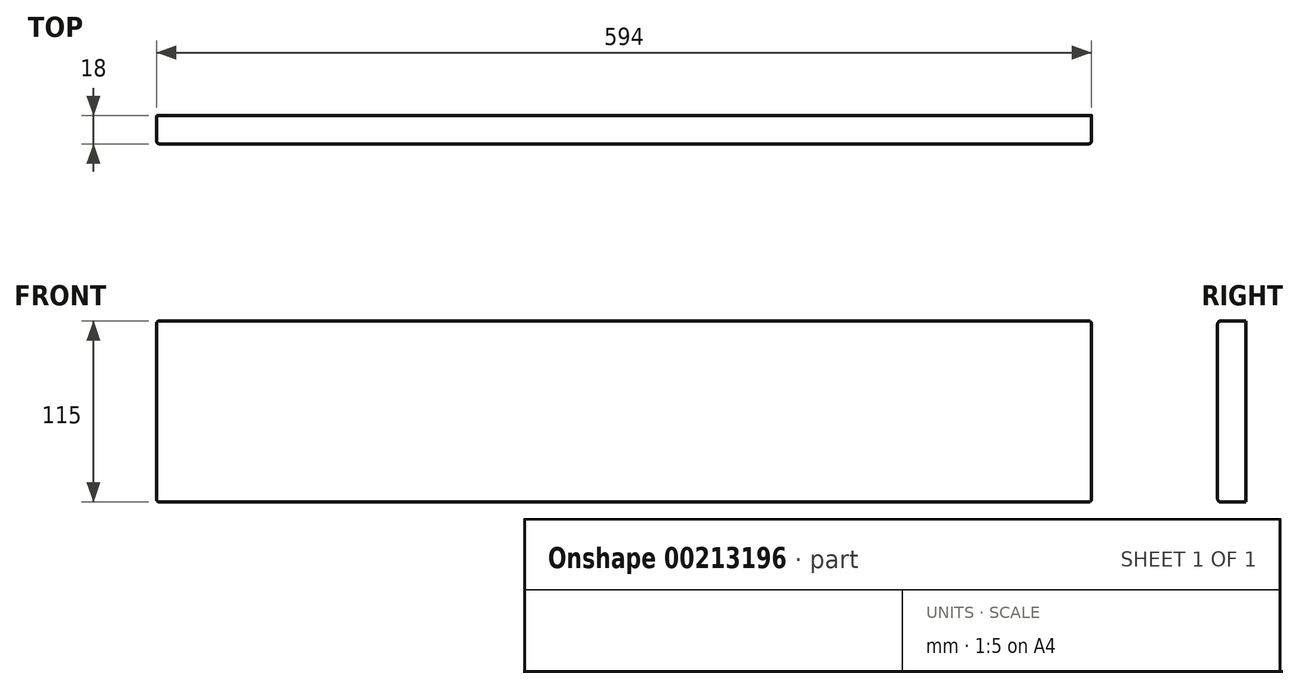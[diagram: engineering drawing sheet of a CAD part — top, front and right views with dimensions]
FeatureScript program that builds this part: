
annotation { "Feature Type Name" : "Feature", "Feature Type Description" : "" }
export const myFeature = defineFeature(function(context is Context, id is Id, definition is map)
    precondition{}
    {
        {
            var Q0;
            Q0=qCreatedBy(makeId("Front.planeOp"),FACE);
            var sketch = newSketch(context, id + "F0", { "sketchPlane" : qUnion([Q0])});
            skLineSegment(sketch, "E0.bottom", {"start": v(297, 57.5) * mm, "end": v(-297, 57.5) * mm});
            skLineSegment(sketch, "E0.top", {"start": v(297, -57.5) * mm, "end": v(-297, -57.5) * mm});
            skLineSegment(sketch, "E0.left", {"start": v(297, 57.5) * mm, "end": v(297, -57.5) * mm});
            skLineSegment(sketch, "E0.right", {"start": v(-297, 57.5) * mm, "end": v(-297, -57.5) * mm});
            skPoint(sketch, "E0.middle", {"position": v(0, 0) * mm});
            skSolve(sketch);
        }
        {
            var Q0;
            Q0=makeQuery(id+"F0.imprint","IMPRINT",FACE,{"disambiguationData":[TD([[makeQuery(id+"F0.imprint","IMPRINT",EDGE,{"derivedFrom":sQuery(id+"F0.wireOp",EDGE,"E0.bottom")}),1.0]])]});
            extrude(context, id + "F1", {"entities" : qUnion([Q0]), "endBound" : BoundingType.SYMMETRIC, "depth" : 18 * mm});
        }
        {
            var Q0;
            Q0=makeQuery(id+"F1.opExtrude","CAP_FACE",FACE,{"disambiguationData":[OSD([sQuery(id+"F0.wireOp",EDGE,"E0.bottom"),sQuery(id+"F0.wireOp",EDGE,"E0.top"),sQuery(id+"F0.wireOp",EDGE,"E0.left"),sQuery(id+"F0.wireOp",EDGE,"E0.right")])],"isStart":false});
            var Q1;
            Q1=makeQuery(id+"F1.opExtrude","SWEPT_EDGE",EDGE,{"disambiguationData":[OSD([sQuery(id+"F0.wireOp",EDGE,"E0.bottom"),sQuery(id+"F0.wireOp",EDGE,"E0.right")])]});
            var Q2;
            Q2=makeQuery(id+"F1.opExtrude","SWEPT_EDGE",EDGE,{"disambiguationData":[OSD([sQuery(id+"F0.wireOp",EDGE,"E0.top"),sQuery(id+"F0.wireOp",EDGE,"E0.right")])]});
            var Q3;
            Q3=makeQuery(id+"F1.opExtrude","SWEPT_EDGE",EDGE,{"disambiguationData":[OSD([sQuery(id+"F0.wireOp",EDGE,"E0.bottom"),sQuery(id+"F0.wireOp",EDGE,"E0.left")])]});
            var Q4;
            Q4=makeQuery(id+"F1.opExtrude","SWEPT_EDGE",EDGE,{"disambiguationData":[OSD([sQuery(id+"F0.wireOp",EDGE,"E0.top"),sQuery(id+"F0.wireOp",EDGE,"E0.left")])]});
            fillet(context, id + "F2", {"entities" : qUnion([Q0, Q1, Q2, Q3, Q4]), "radius" : 2 * mm, "tangentPropagation" : true, "allowEdgeOverflow" : false});
        }
    });
